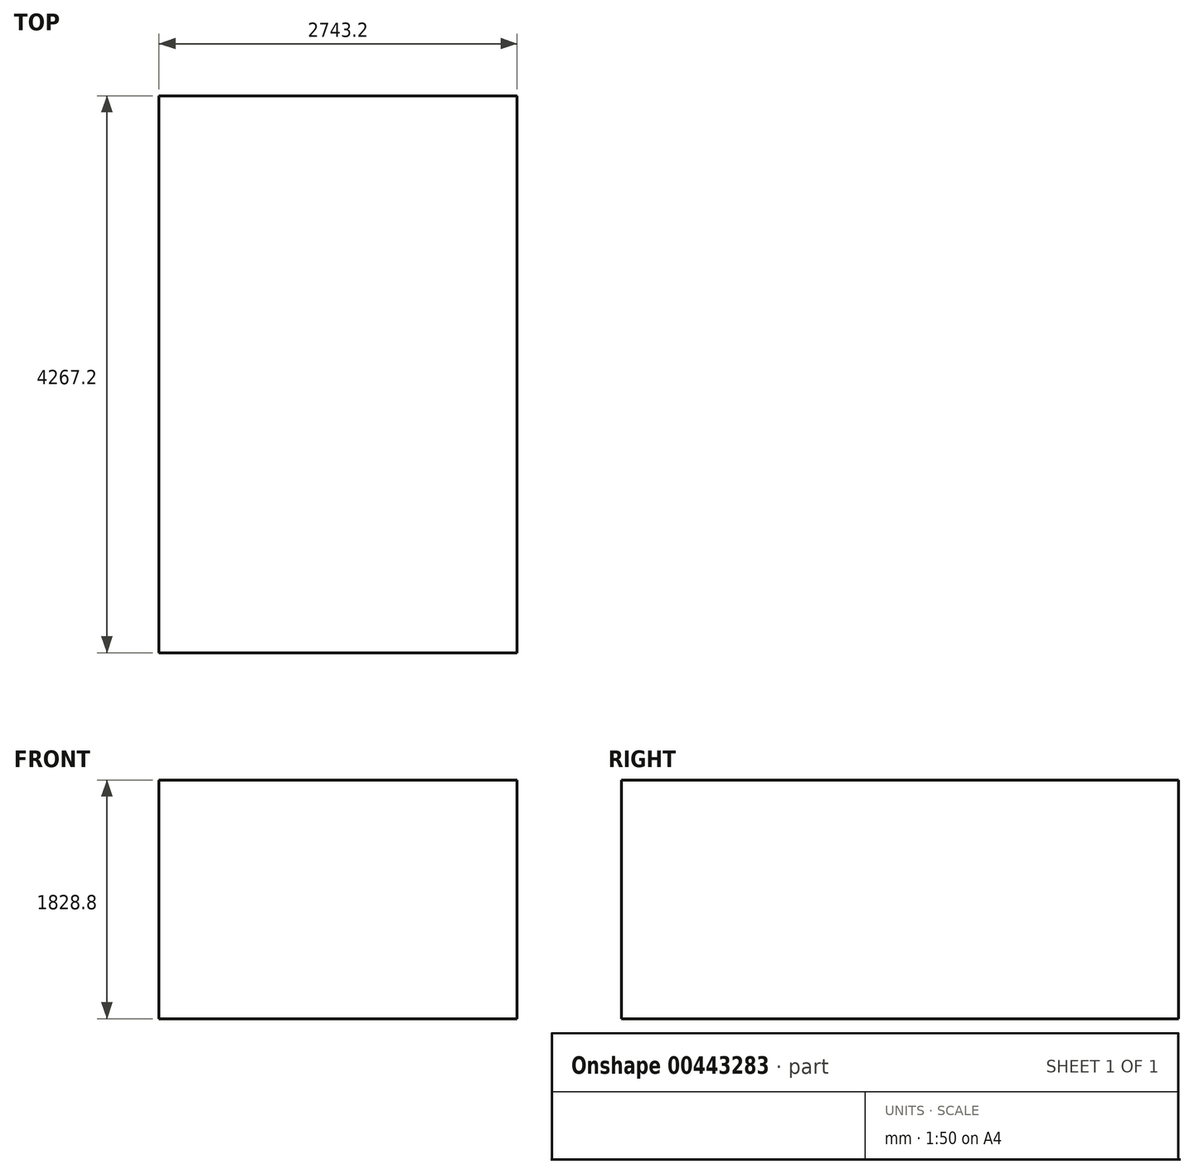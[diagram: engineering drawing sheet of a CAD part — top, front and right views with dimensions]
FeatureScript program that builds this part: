
annotation { "Feature Type Name" : "Feature", "Feature Type Description" : "" }
export const myFeature = defineFeature(function(context is Context, id is Id, definition is map)
    precondition{}
    {
        {
            var Q0;
            Q0=qCreatedBy(makeId("Top.planeOp"),FACE);
            var sketch = newSketch(context, id + "F0", { "sketchPlane" : qUnion([Q0])});
            skLineSegment(sketch, "E0.bottom", {"start": v(-1371.6, 2133.6) * mm, "end": v(1371.6, 2133.6) * mm});
            skLineSegment(sketch, "E0.top", {"start": v(-1371.6, -2133.6) * mm, "end": v(1371.6, -2133.6) * mm});
            skLineSegment(sketch, "E0.left", {"start": v(-1371.6, 2133.6) * mm, "end": v(-1371.6, -2133.6) * mm});
            skLineSegment(sketch, "E0.right", {"start": v(1371.6, 2133.6) * mm, "end": v(1371.6, -2133.6) * mm});
            skPoint(sketch, "E0.middle", {"position": v(0, 0) * mm});
            skSolve(sketch);
        }
        {
            var Q0;
            Q0 = qSketchRegion(id + "F0", true);
            extrude(context, id + "F1", {"entities" : qUnion([Q0]), "depth" : 1828.8 * mm});
        }
    });
